# Revit family: 01-Valvula de descarga - DocolSystem
name_source: partatom
category: Conexões hidráulicas
revit_build: Autodesk Revit MEP 2014 (Build: 20131024_2115(x64)
units: mm (PartAtom-declared; Revit-internal decimal feet)

## types (2) — shared parameters
Conexão CW = Sim
Conexão HW = Sim
Conexão de resíduos = Sim
Conexão de ventilação = Sim
Diâmetro Nominal Saida = 40  [stored 0.131234 ft]
Docol: Acabamento = Ferro
Docol: Ambiente = Banheiro
Docol: Categoria = Sistemas de Descarga
Docol: Fabricante = Docol
Docol: Linha = Válvulas de Descarga DocolBase
Docol: Link do Produto = http://www.docol.com.br
Docol: Temperatura Máxima = 0 °C
Elevação-padrão = 900  [stored 2.95276 ft]
Fabricante = Docol
Raio Nominal Saida = 20  [stored 0.0656168 ft]
URL = www.docol.com.br

## per-type parameters (varying)
| type | Descrição | Diâmetro Nominal Entrada | Docol: Bitola | Docol: Código | Docol: Descrição | Modelo | Raio Nominal Entrada |
| 1 1/2" Baixa Pressão | Válvula de descarga 1 1/2" baixa pressão, DocolSystem | 50  [stored 0.164042 ft] | 1 1/2" | 01021500 | Válvula de descarga 1 1/2" baixa pressão, DocolSystem | 01021500 | 25  [stored 0.082021 ft] |
| 1 1/4" Alta Pressão | Válvula de descarga 1 1/4" alta pressão, DocolSystem | 40  [stored 0.131234 ft] | 1 1/4" | 01051300 | Válvula de descarga 1 1/4" alta pressão, DocolSystem | 01051300 | 20  [stored 0.0656168 ft] |

note: [stored X ft] marks values corroborated as IEEE doubles in the binary element streams (Revit-internal decimal feet)

## geometry (parser evidence)
native form markers: Sweep x1
no freeform markers — native parametric forms only
